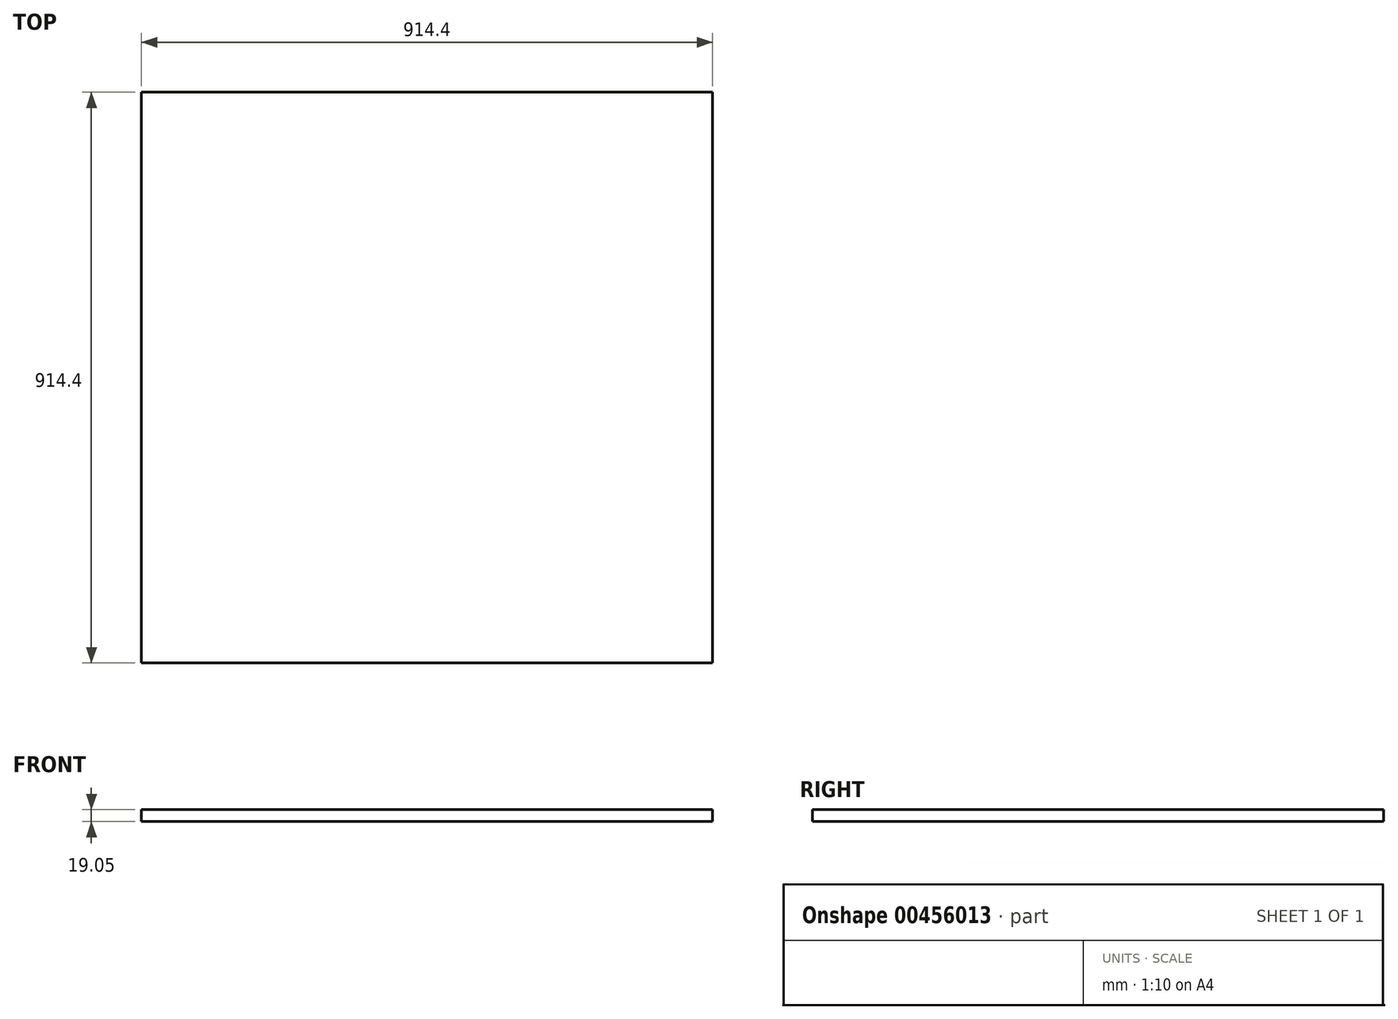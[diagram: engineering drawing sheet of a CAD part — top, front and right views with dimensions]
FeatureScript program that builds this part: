
annotation { "Feature Type Name" : "Feature", "Feature Type Description" : "" }
export const myFeature = defineFeature(function(context is Context, id is Id, definition is map)
    precondition{}
    {
        {
            var Q0;
            Q0=qCreatedBy(makeId("Top.planeOp"),FACE);
            var sketch = newSketch(context, id + "F0", { "sketchPlane" : qUnion([Q0])});
            skLineSegment(sketch, "E0.bottom", {"start": v(-450.45, 626.98) * mm, "end": v(463.95, 626.98) * mm});
            skLineSegment(sketch, "E0.top", {"start": v(-450.45, -287.42) * mm, "end": v(463.95, -287.42) * mm});
            skLineSegment(sketch, "E0.left", {"start": v(-450.45, 626.98) * mm, "end": v(-450.45, -287.42) * mm});
            skLineSegment(sketch, "E0.right", {"start": v(463.95, 626.98) * mm, "end": v(463.95, -287.42) * mm});
            skSolve(sketch);
        }
        {
            var Q0;
            Q0=makeQuery(id+"F0.imprint","IMPRINT",FACE,{"disambiguationData":[TD([[makeQuery(id+"F0.imprint","IMPRINT",EDGE,{"derivedFrom":sQuery(id+"F0.wireOp",EDGE,"E0.bottom")}),-1.0]])]});
            extrude(context, id + "F1", {"entities" : qUnion([Q0]), "depth" : 19.05 * mm});
        }
    });
